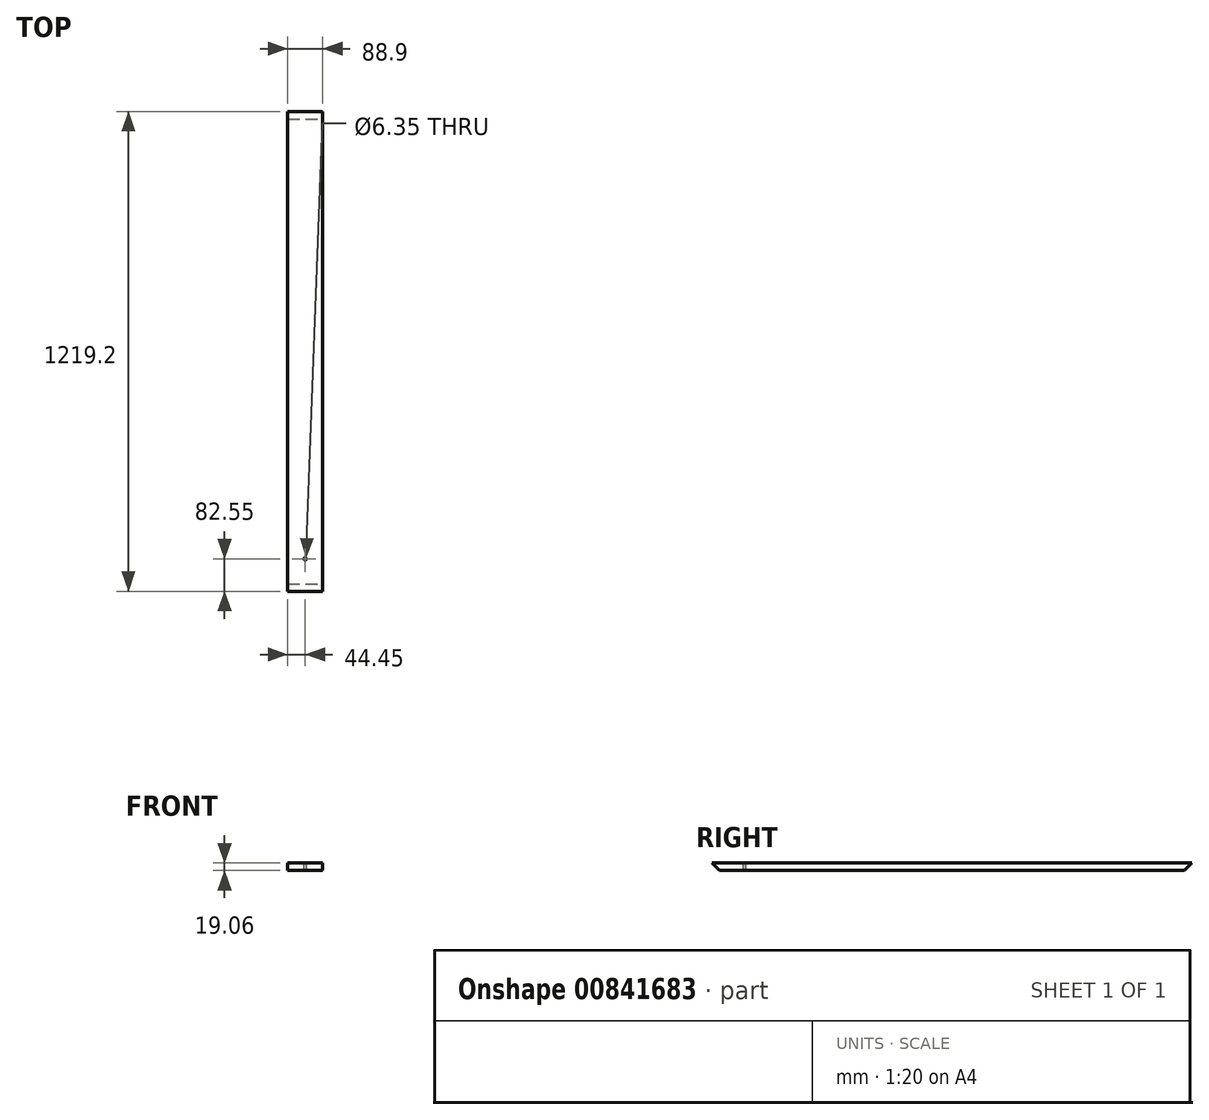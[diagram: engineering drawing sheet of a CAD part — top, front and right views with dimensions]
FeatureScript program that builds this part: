
annotation { "Feature Type Name" : "Feature", "Feature Type Description" : "" }
export const myFeature = defineFeature(function(context is Context, id is Id, definition is map)
    precondition{}
    {
        {
            var Q0;
            Q0=qCreatedBy(makeId("Front.planeOp"),FACE);
            var sketch = newSketch(context, id + "F0", { "sketchPlane" : qUnion([Q0])});
            skLineSegment(sketch, "E0.bottom", {"start": v(44.45, -9.53) * mm, "end": v(-44.45, -9.53) * mm});
            skLineSegment(sketch, "E0.top", {"start": v(44.45, 9.53) * mm, "end": v(-44.45, 9.53) * mm});
            skLineSegment(sketch, "E0.left", {"start": v(44.45, -9.53) * mm, "end": v(44.45, 9.53) * mm});
            skLineSegment(sketch, "E0.right", {"start": v(-44.45, -9.53) * mm, "end": v(-44.45, 9.52) * mm});
            skPoint(sketch, "E0.middle", {"position": v(0, 0) * mm});
            skSolve(sketch);
        }
        {
            var Q0;
            Q0 = qSketchRegion(id + "F0", true);
            extrude(context, id + "F1", {"entities" : qUnion([Q0]), "depth" : 1219.2 * mm, "offsetDistance" : 25.4 * mm});
        }
        {
            var Q0;
            Q0=makeQuery(id+"F1.opExtrude","SWEPT_FACE",FACE,{"disambiguationData":[OSD([sQuery(id+"F0.wireOp",EDGE,"E0.left")])]});
            var sketch = newSketch(context, id + "F2", { "sketchPlane" : qUnion([Q0])});
            skLineSegment(sketch, "E1", {"start": v(0, 9.53) * mm, "end": v(-19.05, -9.52) * mm});
            skLineSegment(sketch, "E2", {"start": v(-19.05, -9.53) * mm, "end": v(0, -9.52) * mm});
            skLineSegment(sketch, "E3", {"start": v(0, -9.52) * mm, "end": v(0, 9.53) * mm});
            skLineSegment(sketch, "E4", {"start": v(-1219.2, 9.52) * mm, "end": v(-1200.15, -9.52) * mm});
            skLineSegment(sketch, "E5", {"start": v(-1200.15, -9.52) * mm, "end": v(-1219.2, -9.52) * mm});
            skLineSegment(sketch, "E6", {"start": v(-1219.2, -9.52) * mm, "end": v(-1219.2, 9.53) * mm});
            skSolve(sketch);
        }
        {
            var Q0;
            Q0 = qSketchRegion(id + "F2", true);
            extrude(context, id + "F3", {"entities" : qUnion([Q0]), "operationType" : NewBodyOperationType.REMOVE, "endBound" : BoundingType.THROUGH_ALL, "oppositeDirection" : true, "depth" : 25.4 * mm, "offsetDistance" : 25.4 * mm});
        }
        {
            var Q0;
            Q0=makeQuery(id+"F1.opExtrude","SWEPT_FACE",FACE,{"disambiguationData":[OSD([sQuery(id+"F0.wireOp",EDGE,"E0.top")])]});
            var sketch = newSketch(context, id + "F4", { "sketchPlane" : qUnion([Q0])});
            skLineSegment(sketch, "E7", {"start": v(-44.45, -1136.65) * mm, "end": v(0, -1136.65) * mm, "construction": true});
            skSolve(sketch);
        }
        {
            var Q0;
            Q0=sQuery(id+"F4.wireOp",VERTEX,"E7.end");
            var Q1;
            Q1=makeQuery(id+"F1.opExtrude","SWEPT_BODY",BODY,{"disambiguationData":[OSD([sQuery(id+"F0.wireOp",EDGE,"E0.bottom"),sQuery(id+"F0.wireOp",EDGE,"E0.top"),sQuery(id+"F0.wireOp",EDGE,"E0.left"),sQuery(id+"F0.wireOp",EDGE,"E0.right")])]});
            hole(context, id + "F5", {"style" : HoleStyle.SIMPLE, "endStyle" : HoleEndStyle.THROUGH, "holeDiameter" : 6.35 * mm, "majorDiameter" : 6.35 * mm, "isTappedThrough" : true, "tappedDepth" : 12.7 * mm, "tapClearance" : 3, "locations" : qUnion([Q0]), "scope" : qUnion([Q1])});
        }
    });
